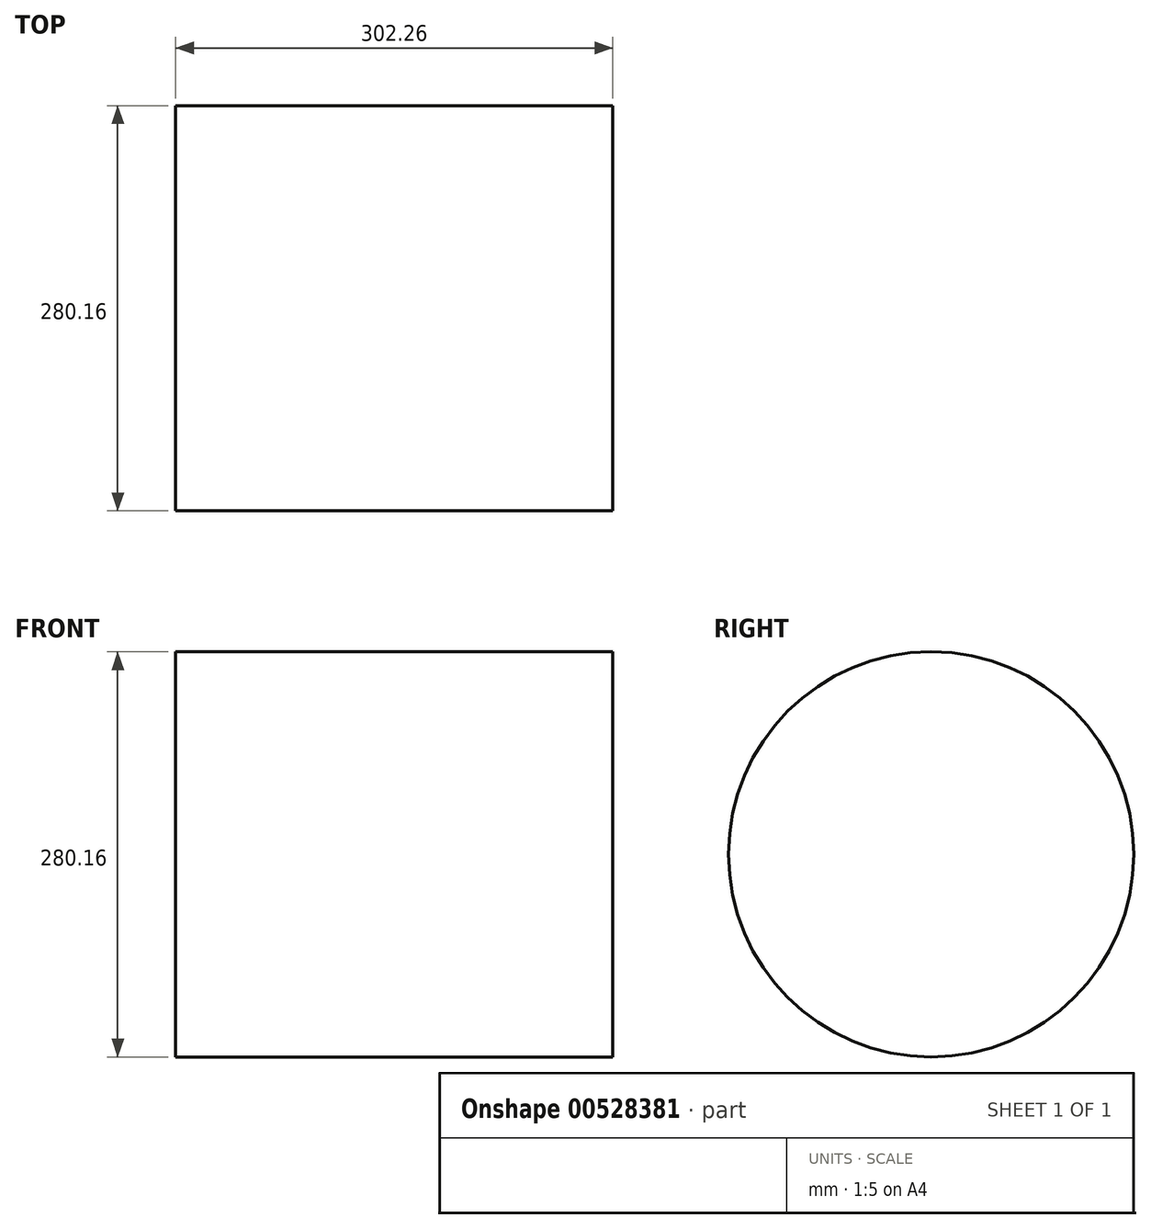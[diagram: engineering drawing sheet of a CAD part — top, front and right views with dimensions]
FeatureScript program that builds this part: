
annotation { "Feature Type Name" : "Feature", "Feature Type Description" : "" }
export const myFeature = defineFeature(function(context is Context, id is Id, definition is map)
    precondition{}
    {
        {
            var Q0;
            Q0=qCreatedBy(makeId("Right.planeOp"),FACE);
            var sketch = newSketch(context, id + "F0", { "sketchPlane" : qUnion([Q0])});
            skCircle(sketch, "E0", {"center": v(465.75, 405.16) * mm, "radius": 140.08 * mm});
            skSolve(sketch);
        }
        {
            var Q0;
            Q0=makeQuery(id+"F0.imprint","IMPRINT",FACE,{"disambiguationData":[TD([[makeQuery(id+"F0.imprint","IMPRINT",EDGE,{"derivedFrom":sQuery(id+"F0.wireOp",EDGE,"E0")}),1.0]])]});
            extrude(context, id + "F1", {"entities" : qUnion([Q0]), "depth" : 302.26 * mm, "offsetDistance" : 25.4 * mm});
        }
    });
